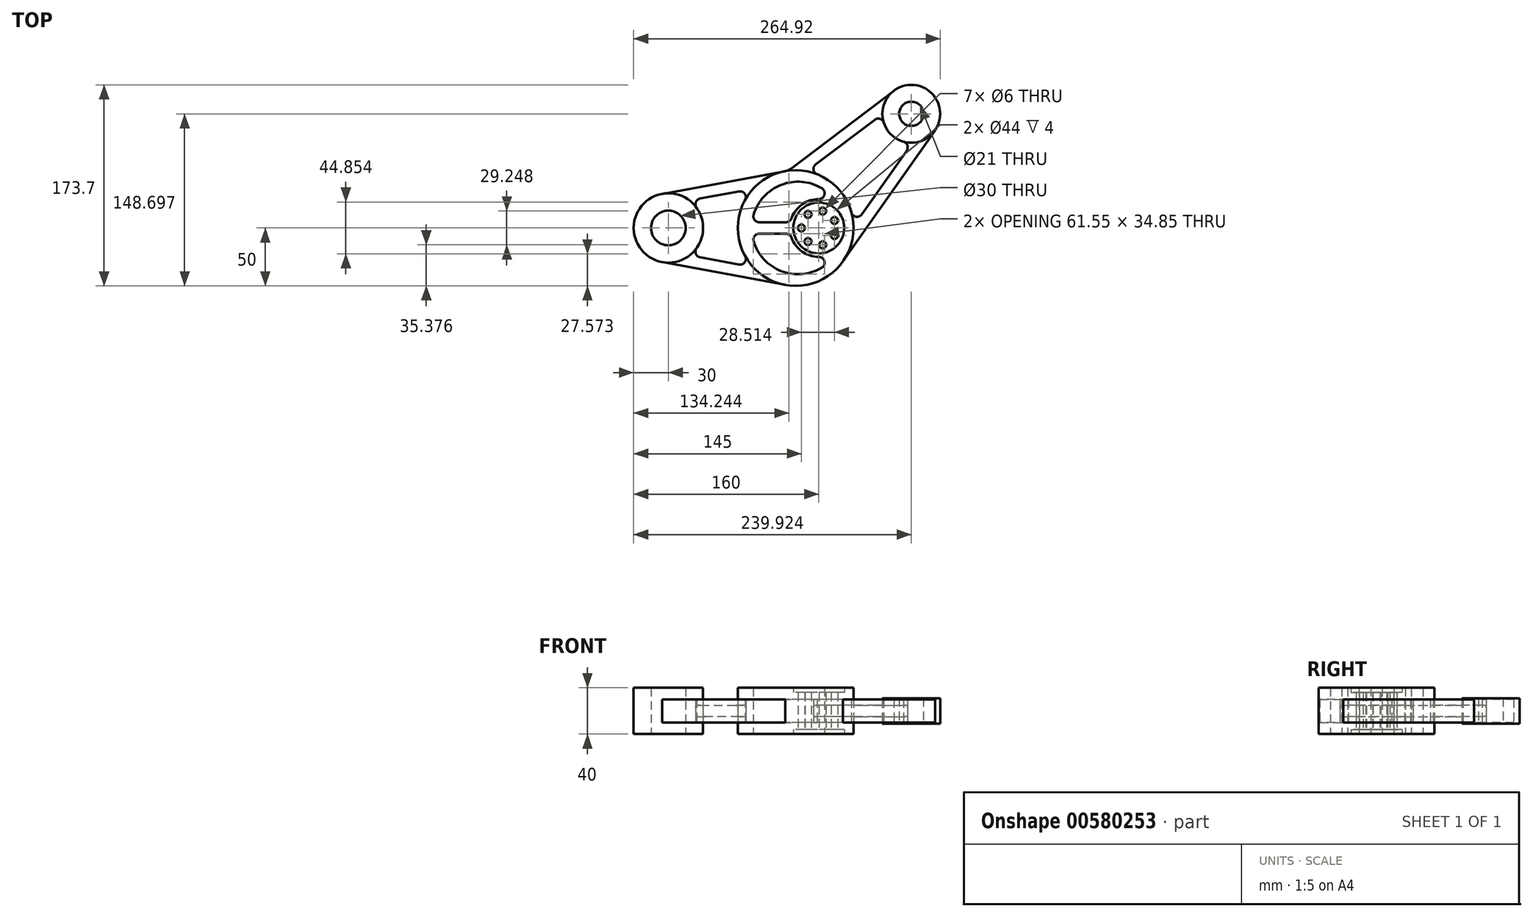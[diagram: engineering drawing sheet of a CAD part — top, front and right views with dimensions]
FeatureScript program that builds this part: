
annotation { "Feature Type Name" : "Feature", "Feature Type Description" : "" }
export const myFeature = defineFeature(function(context is Context, id is Id, definition is map)
    precondition{}
    {
        {
            var Q0;
            Q0=qCreatedBy(makeId("Top.planeOp"),FACE);
            var sketch = newSketch(context, id + "F0", { "sketchPlane" : qUnion([Q0])});
            skCircle(sketch, "E0", {"center": v(0, 0) * mm, "radius": 22 * mm});
            skLineSegment(sketch, "E1", {"start": v(0, 0) * mm, "end": v(90.96, 112.33) * mm, "construction": true});
            skLineSegment(sketch, "E2", {"start": v(0, 0) * mm, "end": v(-193.21, 0) * mm, "construction": true});
            skCircle(sketch, "E3", {"center": v(-130, 0) * mm, "radius": 15 * mm});
            skCircle(sketch, "E4", {"center": v(79.92, 98.7) * mm, "radius": 10.5 * mm});
            skCircle(sketch, "E5", {"center": v(79.92, 98.7) * mm, "radius": 25 * mm});
            skCircle(sketch, "E6", {"center": v(-130, 0) * mm, "radius": 30 * mm});
            skArc(sketch, "E7", {"start": v(0.02, 25) * mm, "mid": v(-14.42, 20.42) * mm, "end": v(-23.57, 8.33) * mm});
            skArc(sketch, "E8", {"start": v(2.6, 34.29) * mm, "mid": v(-32.46, 37.3) * mm, "end": v(-56.33, 11.43) * mm});
            skCircle(sketch, "E9", {"center": v(-20, 0) * mm, "radius": 50 * mm});
            skLineSegment(sketch, "E10.bottom", {"start": v(-28.28, 5) * mm, "end": v(-51.54, 5) * mm});
            skLineSegment(sketch, "E10.top", {"start": v(-28.28, -5) * mm, "end": v(-51.54, -5) * mm});
            skLineSegment(sketch, "E11", {"start": v(20.9, -28.75) * mm, "end": v(100.38, 84.32) * mm});
            skLineSegment(sketch, "E12", {"start": v(-29.1, -49.17) * mm, "end": v(-135.45, -29.5) * mm});
            skArc(sketch, "E13.trimOffspring", {"start": v(-56.33, -11.43) * mm, "mid": v(-32.46, -37.3) * mm, "end": v(2.6, -34.29) * mm});
            skArc(sketch, "E14.trimOffspring", {"start": v(-23.57, -8.33) * mm, "mid": v(-14.42, -20.42) * mm, "end": v(0.02, -25) * mm});
            skPoint(sketch, "E15.visualSharp", {"position": v(-57.69, 5) * mm});
            skArc(sketch, "E15.filletArc", {"start": v(-56.33, 11.43) * mm, "mid": v(-55.55, 7.01) * mm, "end": v(-51.54, 5) * mm});
            skPoint(sketch, "E16.visualSharp", {"position": v(18.08, 17.26) * mm});
            skArc(sketch, "E16.filletArc", {"start": v(0.02, 25) * mm, "mid": v(4.85, 28.66) * mm, "end": v(2.6, 34.29) * mm});
            skPoint(sketch, "E17.visualSharp", {"position": v(18.08, -17.26) * mm});
            skArc(sketch, "E17.filletArc", {"start": v(2.6, -34.29) * mm, "mid": v(4.85, -28.66) * mm, "end": v(0.02, -25) * mm});
            skPoint(sketch, "E18.visualSharp", {"position": v(-57.69, -5) * mm});
            skArc(sketch, "E18.filletArc", {"start": v(-51.54, -5) * mm, "mid": v(-55.55, -7.01) * mm, "end": v(-56.33, -11.43) * mm});
            skPoint(sketch, "E19.visualSharp", {"position": v(-24.5, 5) * mm});
            skArc(sketch, "E19.filletArc", {"start": v(-28.28, 5) * mm, "mid": v(-25.4, 5.92) * mm, "end": v(-23.57, 8.33) * mm});
            skPoint(sketch, "E20.visualSharp", {"position": v(-24.5, -5) * mm});
            skArc(sketch, "E20.filletArc", {"start": v(-23.57, -8.33) * mm, "mid": v(-25.4, -5.92) * mm, "end": v(-28.28, -5) * mm});
            skCircle(sketch, "E21", {"center": v(0, 0) * mm, "radius": 15 * mm, "construction": true});
            skCircle(sketch, "E22", {"center": v(-15, 0) * mm, "radius": 3 * mm});
            skCircle(sketch, "E23.1.0", {"center": v(-9.35, -11.73) * mm, "radius": 3 * mm});
            skCircle(sketch, "E23.2.0", {"center": v(3.34, -14.62) * mm, "radius": 3 * mm});
            skCircle(sketch, "E23.3.0", {"center": v(13.51, -6.5) * mm, "radius": 3 * mm});
            skCircle(sketch, "E23.4.0", {"center": v(13.51, 6.5) * mm, "radius": 3 * mm});
            skCircle(sketch, "E23.5.0", {"center": v(3.34, 14.62) * mm, "radius": 3 * mm});
            skCircle(sketch, "E23.6.0", {"center": v(-9.35, 11.73) * mm, "radius": 3 * mm});
            skLineSegment(sketch, "E24", {"start": v(-135.45, 29.5) * mm, "end": v(-29.1, 49.17) * mm});
            skLineSegment(sketch, "E25", {"start": v(64.84, 118.63) * mm, "end": v(-24.03, 51.4) * mm});
            skArc(sketch, "E26.filletArc", {"start": v(-29.1, 49.17) * mm, "mid": v(-26.43, 49.99) * mm, "end": v(-24.03, 51.4) * mm});
            skLineSegment(sketch, "E27.0", {"start": v(-102.54, 25.42) * mm, "end": v(-69, 31.62) * mm});
            skLineSegment(sketch, "E28.0", {"start": v(-69, -31.62) * mm, "end": v(-102.54, -25.42) * mm});
            skLineSegment(sketch, "E29.0", {"start": v(48.32, 93.6) * mm, "end": v(-2.61, 55.06) * mm});
            skArc(sketch, "E30", {"start": v(-102.54, 25.42) * mm, "mid": v(-106.27, 22.36) * mm, "end": v(-105.68, 17.57) * mm});
            skArc(sketch, "E31", {"start": v(-63.71, 24.28) * mm, "mid": v(-64.02, 29.62) * mm, "end": v(-69, 31.62) * mm});
            skArc(sketch, "E32", {"start": v(-2.61, 55.06) * mm, "mid": v(-4.55, 50.4) * mm, "end": v(-1.45, 46.43) * mm});
            skArc(sketch, "E33", {"start": v(56.1, 91.12) * mm, "mid": v(52.85, 94.37) * mm, "end": v(48.32, 93.6) * mm});
            skArc(sketch, "E34", {"start": v(-105.68, -17.57) * mm, "mid": v(-106.27, -22.36) * mm, "end": v(-102.54, -25.42) * mm});
            skArc(sketch, "E35", {"start": v(-69, -31.62) * mm, "mid": v(-64.02, -29.62) * mm, "end": v(-63.71, -24.28) * mm});
            skLineSegment(sketch, "E36.0", {"start": v(37.12, 11.71) * mm, "end": v(75.93, 66.93) * mm});
            skArc(sketch, "E37", {"start": v(28.2, 13.26) * mm, "mid": v(32.17, 9.66) * mm, "end": v(37.12, 11.71) * mm});
            skArc(sketch, "E38", {"start": v(75.93, 66.93) * mm, "mid": v(76.55, 71.49) * mm, "end": v(73.19, 74.62) * mm});
            skSolve(sketch);
        }
        {
            var Q0;
            Q0=makeQuery(id+"F0.imprint","IMPRINT",FACE,{"disambiguationData":[TD([[makeQuery(id+"F0.imprint","IMPRINT",EDGE,{"derivedFrom":sQuery(id+"F0.wireOp",EDGE,"E3")}),-1.0]])]});
            var Q1;
            Q1=makeQuery(id+"F0.imprint","IMPRINT",FACE,{"disambiguationData":[TD([[makeQuery(id+"F0.imprint","IMPRINT",EDGE,{"derivedFrom":sQuery(id+"F0.wireOp",EDGE,"E0")}),-1.0]])]});
            extrude(context, id + "F1", {"entities" : qUnion([Q0, Q1]), "endBound" : BoundingType.SYMMETRIC, "depth" : 40 * mm, "offsetDistance" : 25 * mm});
        }
        {
            var Q0;
            {var subQ0=sQuery(id+"F0.wireOp",EDGE,"E24");Q0=makeQuery(id+"F0.imprint","IMPRINT",FACE,{"disambiguationData":[TD([[makeQuery(id+"F0.imprint","IMPRINT",EDGE,{"derivedFrom":subQ0}),-1.0]])]});}
            var Q1;
            {var subQ0=sQuery(id+"F0.wireOp",EDGE,"E12");Q1=makeQuery(id+"F0.imprint","IMPRINT",FACE,{"disambiguationData":[TD([[makeQuery(id+"F0.imprint","IMPRINT",EDGE,{"derivedFrom":subQ0}),-1.0]])]});}
            var Q2;
            {var subQ1=sQuery(id+"F0.wireOp",EDGE,"E25");Q2=makeQuery(id+"F0.imprint","IMPRINT",FACE,{"disambiguationData":[TD([[makeQuery(id+"F0.imprint","IMPRINT",EDGE,{"derivedFrom":subQ1}),1.0]])]});}
            var Q3;
            {var subQ0=sQuery(id+"F0.wireOp",EDGE,"E11");Q3=makeQuery(id+"F0.imprint","IMPRINT",FACE,{"disambiguationData":[TD([[makeQuery(id+"F0.imprint","IMPRINT",EDGE,{"derivedFrom":subQ0}),1.0]])]});}
            extrude(context, id + "F2", {"entities" : qUnion([Q0, Q1, Q2, Q3]), "endBound" : BoundingType.SYMMETRIC, "depth" : 20 * mm, "offsetDistance" : 25 * mm});
        }
        {
            var Q0;
            Q0=makeQuery(id+"F0.imprint","IMPRINT",FACE,{"disambiguationData":[TD([[makeQuery(id+"F0.imprint","IMPRINT",EDGE,{"derivedFrom":sQuery(id+"F0.wireOp",EDGE,"E27.0")}),-1.0]])]});
            var Q1;
            Q1=makeQuery(id+"F0.imprint","IMPRINT",FACE,{"disambiguationData":[TD([[makeQuery(id+"F0.imprint","IMPRINT",EDGE,{"derivedFrom":sQuery(id+"F0.wireOp",EDGE,"E29.0")}),1.0]])]});
            extrude(context, id + "F3", {"entities" : qUnion([Q0, Q1]), "endBound" : BoundingType.SYMMETRIC, "depth" : 10 * mm, "offsetDistance" : 25 * mm});
        }
        {
            var Q0;
            Q0=makeQuery(id+"F0.imprint","IMPRINT",FACE,{"disambiguationData":[TD([[makeQuery(id+"F0.imprint","IMPRINT",EDGE,{"derivedFrom":sQuery(id+"F0.wireOp",EDGE,"E0")}),1.0]])]});
            extrude(context, id + "F4", {"entities" : qUnion([Q0]), "operationType" : NewBodyOperationType.ADD, "endBound" : BoundingType.SYMMETRIC, "depth" : 32 * mm, "offsetDistance" : 25 * mm});
        }
        {
            var Q0;
            Q0=makeQuery(id+"F0.imprint","IMPRINT",FACE,{"disambiguationData":[TD([[makeQuery(id+"F0.imprint","IMPRINT",EDGE,{"derivedFrom":sQuery(id+"F0.wireOp",EDGE,"E4")}),-1.0]])]});
            extrude(context, id + "F5", {"entities" : qUnion([Q0]), "endBound" : BoundingType.SYMMETRIC, "depth" : 22 * mm, "offsetDistance" : 25 * mm});
        }
        {
            var Q0;
            Q0=makeQuery(id+"F3.opExtrude","CAP_EDGE",EDGE,{"disambiguationData":[OSD([sQuery(id+"F0.wireOp",EDGE,"E27.0")])],"isStart":false});
            var Q1;
            Q1=makeQuery(id+"F3.opExtrude","CAP_EDGE",EDGE,{"disambiguationData":[OSD([sQuery(id+"F0.wireOp",EDGE,"E29.0")])],"isStart":false});
            var Q2;
            Q2=makeQuery(id+"F3.opExtrude","CAP_EDGE",EDGE,{"disambiguationData":[OSD([sQuery(id+"F0.wireOp",EDGE,"E36.0")])],"isStart":true});
            var Q3;
            Q3=makeQuery(id+"F3.opExtrude","CAP_EDGE",EDGE,{"disambiguationData":[OSD([sQuery(id+"F0.wireOp",EDGE,"E28.0")])],"isStart":true});
            fillet(context, id + "F6", {"entities" : qUnion([Q0, Q1, Q2, Q3]), "radius" : 2 * mm, "tangentPropagation" : true, "allowEdgeOverflow" : false});
        }
    });
